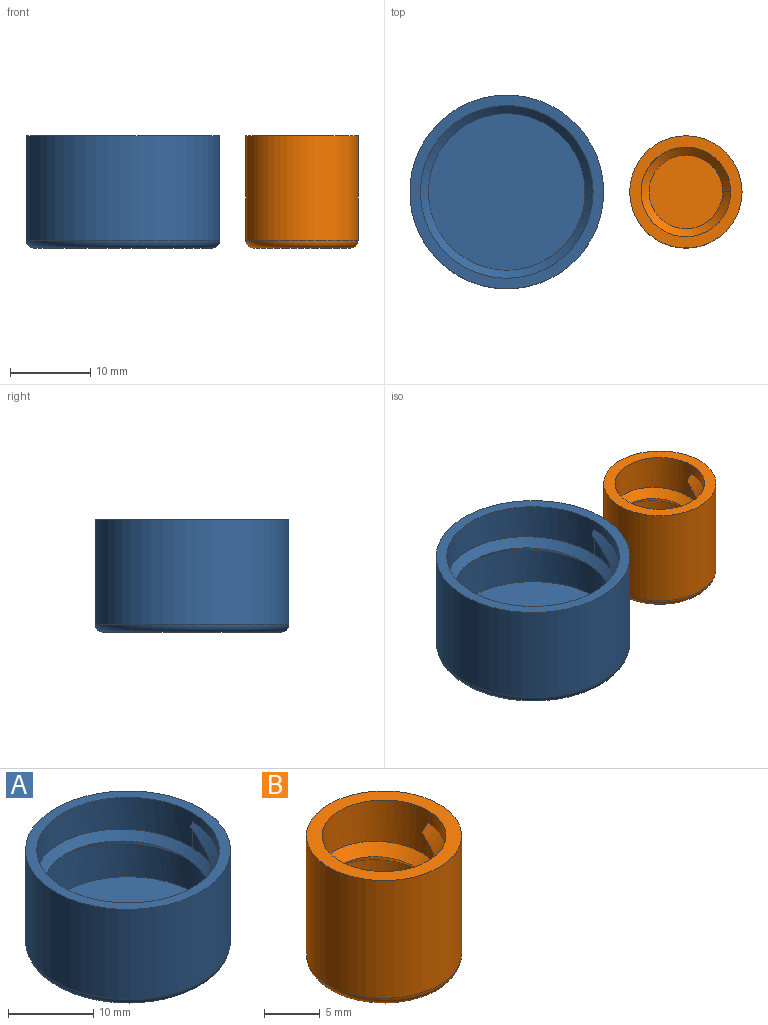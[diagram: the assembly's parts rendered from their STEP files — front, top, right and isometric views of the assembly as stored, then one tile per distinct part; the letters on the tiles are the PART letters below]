
ASSEMBLY  parts=2 mates=1
PART A: 12 faces, bbox 26.1x26.1x14 mm
  f0: cylinder r=12.06mm len=24.13mm, axis (0,0,-1), area 983.2mm2, adj f2,f3
  f1: plane 22.13x22.13mm, normal (0,0,-1), area 384.6mm2, adj f2
  f2: torus R=11.06mm, axis (0,0,1), area 115.5mm2, adj f0,f1
  f3: plane 24.13x24.13mm, normal (0,0,1), area 94.3mm2, adj f0,f11
  f4: plane 0.86x0.45mm, normal (0,1,0), area 0.2mm2, adj f5,f8,f11
  f5: bspline ~3.49x2.35mm, area 3.8mm2, adj f4,f6,f8,f10
  f6: bspline ~24.83x21.5mm, area 116.5mm2, adj f5,f7,f8,f10
  f7: plane 2x0.87mm, normal (-0.87,0.5,0), area 1mm2, adj f6,f8,f10
  f8: bspline ~24.83x21.5mm, area 120.1mm2, adj f4,f5,f6,f7,f10,f11
  f9: plane 21.5x21.5mm, normal (0,0,1), area 363.1mm2, adj f10
  f10: cylinder r=10.75mm len=21.5mm, axis (0,0,-1), area 379.6mm2, adj f5,f6,f7,f8,f9,f11
  f11: cylinder r=10.75mm len=21.5mm, axis (0,0,-1), area 214.5mm2, adj f3,f4,f8,f10
PART B: 12 faces, bbox 15.2x15.2x14 mm
  f0: cylinder r=6.99mm len=13.97mm, axis (0,0,-1), area 569.2mm2, adj f2,f3
  f1: plane 11.97x11.97mm, normal (0,0,-1), area 112.5mm2, adj f2
  f2: torus R=5.98mm, axis (0,0,1), area 65.4mm2, adj f0,f1
  f3: plane 13.97x13.97mm, normal (0,0,1), area 55.5mm2, adj f0,f11
  f4: plane 1.39x0.81mm, normal (0,1,0), area 0.5mm2, adj f5,f8,f11
  f5: bspline ~3.23x2.71mm, area 4.3mm2, adj f4,f6,f8,f10,f11
  f6: bspline ~12.89x11.16mm, area 55.6mm2, adj f5,f7,f8,f10
  f7: plane 2x0.87mm, normal (-0.87,0.5,0), area 1mm2, adj f6,f8,f10
  f8: bspline ~12.89x11.16mm, area 59.9mm2, adj f4,f5,f6,f7,f10,f11
  f9: plane 11.16x11.16mm, normal (0,0,1), area 97.8mm2, adj f10
  f10: cylinder r=5.58mm len=11.16mm, axis (0,0,-1), area 197mm2, adj f5,f6,f7,f8,f9,f11
  f11: cylinder r=5.58mm len=11.16mm, axis (0,0,-1), area 148.6mm2, adj f3,f4,f5,f8,f10
PLACE A at identity
PLACE B t=(22.3,0,0)mm
MATE planar B.f0 <-> A.f0  axis (0,0,-1) through (22.3,0,0)mm
